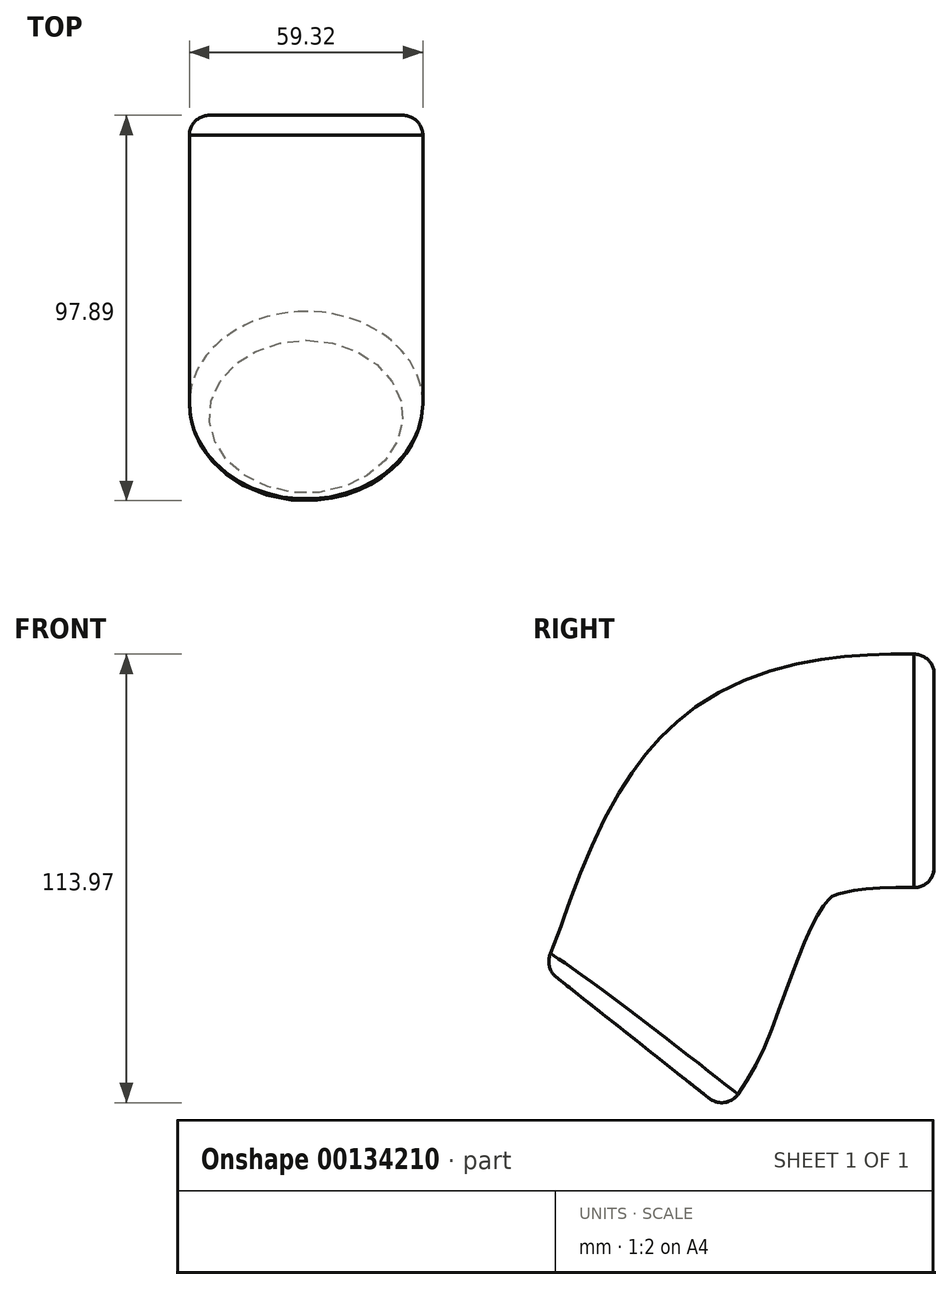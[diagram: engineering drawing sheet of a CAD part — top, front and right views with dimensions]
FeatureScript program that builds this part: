
annotation { "Feature Type Name" : "Feature", "Feature Type Description" : "" }
export const myFeature = defineFeature(function(context is Context, id is Id, definition is map)
    precondition{}
    {
        {
            var Q0;
            Q0=qCreatedBy(makeId("Front.planeOp"),FACE);
            var sketch = newSketch(context, id + "F0", { "sketchPlane" : qUnion([Q0])});
            skCircle(sketch, "E0", {"center": v(0, 0) * mm, "radius": 29.66 * mm});
            skSolve(sketch);
        }
        {
            var Q0;
            Q0=qCreatedBy(makeId("Right.planeOp"),FACE);
            var sketch = newSketch(context, id + "F1", { "sketchPlane" : qUnion([Q0])});
            skFitSpline(sketch, "E1", {"points": [v(0, 0) * mm, v(-46.87, -10.8) * mm, v(-69.94, -57.46) * mm, v(-76.33, -67.96) * mm], "startDerivative": vector(-133.98, 1.28) * mm, "endDerivative": vector(-30.68, -37.97) * mm});
            skSolve(sketch);
        }
        {
            var Q0;
            Q0=makeQuery(id+"F0.imprint","IMPRINT",FACE,{"disambiguationData":[TD([[makeQuery(id+"F0.imprint","IMPRINT",EDGE,{"derivedFrom":sQuery(id+"F0.wireOp",EDGE,"E0")}),1.0]])]});
            var Q1;
            Q1=sQuery(id+"F1.wireOp",EDGE,"E1");
            sweep(context, id + "F2", {"profiles" : qUnion([Q0]), "path" : qUnion([Q1])});
        }
        {
            var Q0;
            Q0=makeQuery(id+"F2.opSweep","CAP_EDGE",EDGE,{"disambiguationData":[OSD([sQuery(id+"F0.wireOp",EDGE,"E0"),sQuery(id+"F1.wireOp",VERTEX,"E1.start")])],"isStart":true});
            fillet(context, id + "F3", {"entities" : qUnion([Q0]), "radius" : 5.08 * mm, "tangentPropagation" : true, "allowEdgeOverflow" : false});
        }
        {
            var Q0;
            Q0=makeQuery(id+"F2.opSweep","CAP_EDGE",EDGE,{"disambiguationData":[OSD([sQuery(id+"F0.wireOp",EDGE,"E0"),sQuery(id+"F1.wireOp",VERTEX,"E1.end")])],"isStart":false});
            fillet(context, id + "F4", {"entities" : qUnion([Q0]), "radius" : 5.08 * mm, "tangentPropagation" : true, "allowEdgeOverflow" : false});
        }
    });
